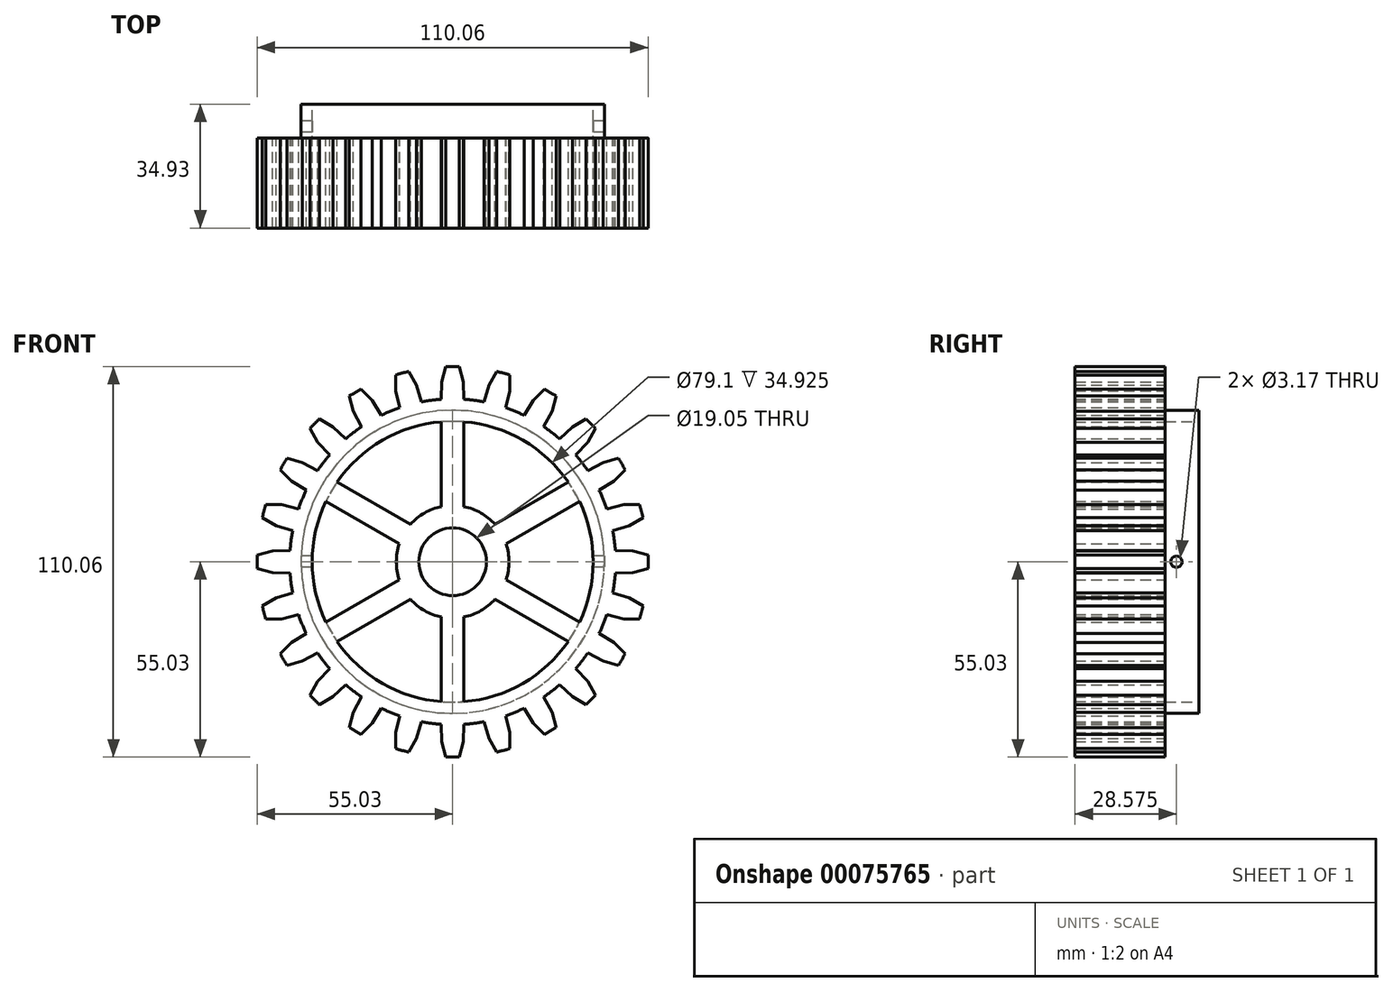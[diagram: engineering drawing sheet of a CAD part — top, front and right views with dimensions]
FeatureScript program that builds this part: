
annotation { "Feature Type Name" : "Feature", "Feature Type Description" : "" }
export const myFeature = defineFeature(function(context is Context, id is Id, definition is map)
    precondition{}
    {
        {
            var Q0;
            Q0=qCreatedBy(makeId("Front.planeOp"),FACE);
            var sketch = newSketch(context, id + "F0", { "sketchPlane" : qUnion([Q0])});
            skCircle(sketch, "E0", {"center": v(0, 0) * mm, "radius": 50.8 * mm, "construction": true});
            skCircle(sketch, "E1", {"center": v(0, 0) * mm, "radius": 45.9 * mm});
            skCircle(sketch, "E2", {"center": v(0, 0) * mm, "radius": 55.03 * mm});
            skLineSegment(sketch, "E3", {"start": v(-3.17, 45.8) * mm, "end": v(-3.05, 50.7) * mm});
            skLineSegment(sketch, "E4", {"start": v(-3.05, 50.7) * mm, "end": v(-1.9, 55) * mm});
            skLineSegment(sketch, "E5", {"start": v(3.18, 45.8) * mm, "end": v(3.05, 50.7) * mm});
            skLineSegment(sketch, "E6", {"start": v(3.05, 50.7) * mm, "end": v(1.9, 55) * mm});
            skLineSegment(sketch, "E7.1.0", {"start": v(-8.79, 45.05) * mm, "end": v(-10.18, 49.77) * mm});
            skLineSegment(sketch, "E7.1.1", {"start": v(-14.92, 43.41) * mm, "end": v(-16.07, 48.2) * mm});
            skLineSegment(sketch, "E7.1.2", {"start": v(-16.07, 48.2) * mm, "end": v(-16.08, 52.63) * mm});
            skLineSegment(sketch, "E7.1.3", {"start": v(-10.18, 49.77) * mm, "end": v(-12.4, 53.62) * mm});
            skLineSegment(sketch, "E7.2.0", {"start": v(-20.15, 41.24) * mm, "end": v(-22.71, 45.44) * mm});
            skLineSegment(sketch, "E7.2.1", {"start": v(-25.65, 38.07) * mm, "end": v(-28, 42.4) * mm});
            skLineSegment(sketch, "E7.2.2", {"start": v(-28, 42.4) * mm, "end": v(-29.15, 46.68) * mm});
            skLineSegment(sketch, "E7.2.3", {"start": v(-22.71, 45.44) * mm, "end": v(-25.85, 48.58) * mm});
            skLineSegment(sketch, "E7.3.0", {"start": v(-30.13, 34.62) * mm, "end": v(-33.7, 38.01) * mm});
            skLineSegment(sketch, "E7.3.1", {"start": v(-34.62, 30.13) * mm, "end": v(-38.01, 33.7) * mm});
            skLineSegment(sketch, "E7.3.2", {"start": v(-38.01, 33.7) * mm, "end": v(-40.24, 37.54) * mm});
            skLineSegment(sketch, "E7.3.3", {"start": v(-33.7, 38.01) * mm, "end": v(-37.54, 40.24) * mm});
            skLineSegment(sketch, "E7.4.0", {"start": v(-38.07, 25.65) * mm, "end": v(-42.4, 28) * mm});
            skLineSegment(sketch, "E7.4.1", {"start": v(-41.24, 20.15) * mm, "end": v(-45.44, 22.71) * mm});
            skLineSegment(sketch, "E7.4.2", {"start": v(-45.44, 22.71) * mm, "end": v(-48.58, 25.85) * mm});
            skLineSegment(sketch, "E7.4.3", {"start": v(-42.4, 28) * mm, "end": v(-46.68, 29.15) * mm});
            skLineSegment(sketch, "E7.5.0", {"start": v(-43.41, 14.92) * mm, "end": v(-48.2, 16.07) * mm});
            skLineSegment(sketch, "E7.5.1", {"start": v(-45.05, 8.79) * mm, "end": v(-49.77, 10.18) * mm});
            skLineSegment(sketch, "E7.5.2", {"start": v(-49.77, 10.18) * mm, "end": v(-53.62, 12.4) * mm});
            skLineSegment(sketch, "E7.5.3", {"start": v(-48.2, 16.07) * mm, "end": v(-52.63, 16.08) * mm});
            skLineSegment(sketch, "E7.6.0", {"start": v(-45.8, 3.18) * mm, "end": v(-50.7, 3.05) * mm});
            skLineSegment(sketch, "E7.6.1", {"start": v(-45.8, -3.17) * mm, "end": v(-50.7, -3.05) * mm});
            skLineSegment(sketch, "E7.6.2", {"start": v(-50.7, -3.05) * mm, "end": v(-55, -1.9) * mm});
            skLineSegment(sketch, "E7.6.3", {"start": v(-50.7, 3.05) * mm, "end": v(-55, 1.9) * mm});
            skLineSegment(sketch, "E7.7.0", {"start": v(-45.05, -8.79) * mm, "end": v(-49.77, -10.18) * mm});
            skLineSegment(sketch, "E7.7.1", {"start": v(-43.41, -14.92) * mm, "end": v(-48.2, -16.07) * mm});
            skLineSegment(sketch, "E7.7.2", {"start": v(-48.2, -16.07) * mm, "end": v(-52.63, -16.08) * mm});
            skLineSegment(sketch, "E7.7.3", {"start": v(-49.77, -10.18) * mm, "end": v(-53.62, -12.4) * mm});
            skLineSegment(sketch, "E7.8.0", {"start": v(-41.24, -20.15) * mm, "end": v(-45.44, -22.71) * mm});
            skLineSegment(sketch, "E7.8.1", {"start": v(-38.07, -25.65) * mm, "end": v(-42.4, -28) * mm});
            skLineSegment(sketch, "E7.8.2", {"start": v(-42.4, -28) * mm, "end": v(-46.68, -29.15) * mm});
            skLineSegment(sketch, "E7.8.3", {"start": v(-45.44, -22.71) * mm, "end": v(-48.58, -25.85) * mm});
            skLineSegment(sketch, "E7.9.0", {"start": v(-34.62, -30.13) * mm, "end": v(-38.01, -33.7) * mm});
            skLineSegment(sketch, "E7.9.1", {"start": v(-30.13, -34.62) * mm, "end": v(-33.7, -38.01) * mm});
            skLineSegment(sketch, "E7.9.2", {"start": v(-33.7, -38.01) * mm, "end": v(-37.54, -40.24) * mm});
            skLineSegment(sketch, "E7.9.3", {"start": v(-38.01, -33.7) * mm, "end": v(-40.24, -37.54) * mm});
            skLineSegment(sketch, "E7.10.0", {"start": v(-25.65, -38.07) * mm, "end": v(-28, -42.4) * mm});
            skLineSegment(sketch, "E7.10.1", {"start": v(-20.15, -41.24) * mm, "end": v(-22.71, -45.44) * mm});
            skLineSegment(sketch, "E7.10.2", {"start": v(-22.71, -45.44) * mm, "end": v(-25.85, -48.58) * mm});
            skLineSegment(sketch, "E7.10.3", {"start": v(-28, -42.4) * mm, "end": v(-29.15, -46.68) * mm});
            skLineSegment(sketch, "E7.11.0", {"start": v(-14.92, -43.41) * mm, "end": v(-16.07, -48.2) * mm});
            skLineSegment(sketch, "E7.11.1", {"start": v(-8.79, -45.05) * mm, "end": v(-10.18, -49.77) * mm});
            skLineSegment(sketch, "E7.11.2", {"start": v(-10.18, -49.77) * mm, "end": v(-12.4, -53.62) * mm});
            skLineSegment(sketch, "E7.11.3", {"start": v(-16.07, -48.2) * mm, "end": v(-16.08, -52.63) * mm});
            skLineSegment(sketch, "E7.12.0", {"start": v(-3.18, -45.8) * mm, "end": v(-3.05, -50.7) * mm});
            skLineSegment(sketch, "E7.12.1", {"start": v(3.17, -45.8) * mm, "end": v(3.05, -50.7) * mm});
            skLineSegment(sketch, "E7.12.2", {"start": v(3.05, -50.7) * mm, "end": v(1.9, -55) * mm});
            skLineSegment(sketch, "E7.12.3", {"start": v(-3.05, -50.7) * mm, "end": v(-1.9, -55) * mm});
            skLineSegment(sketch, "E7.13.0", {"start": v(8.79, -45.05) * mm, "end": v(10.18, -49.77) * mm});
            skLineSegment(sketch, "E7.13.1", {"start": v(14.92, -43.41) * mm, "end": v(16.07, -48.2) * mm});
            skLineSegment(sketch, "E7.13.2", {"start": v(16.07, -48.2) * mm, "end": v(16.08, -52.63) * mm});
            skLineSegment(sketch, "E7.13.3", {"start": v(10.18, -49.77) * mm, "end": v(12.4, -53.62) * mm});
            skLineSegment(sketch, "E7.14.0", {"start": v(20.15, -41.24) * mm, "end": v(22.71, -45.44) * mm});
            skLineSegment(sketch, "E7.14.1", {"start": v(25.65, -38.07) * mm, "end": v(28, -42.4) * mm});
            skLineSegment(sketch, "E7.14.2", {"start": v(28, -42.4) * mm, "end": v(29.15, -46.68) * mm});
            skLineSegment(sketch, "E7.14.3", {"start": v(22.71, -45.44) * mm, "end": v(25.85, -48.58) * mm});
            skLineSegment(sketch, "E7.15.0", {"start": v(30.13, -34.62) * mm, "end": v(33.7, -38.01) * mm});
            skLineSegment(sketch, "E7.15.1", {"start": v(34.62, -30.13) * mm, "end": v(38.01, -33.7) * mm});
            skLineSegment(sketch, "E7.15.2", {"start": v(38.01, -33.7) * mm, "end": v(40.24, -37.54) * mm});
            skLineSegment(sketch, "E7.15.3", {"start": v(33.7, -38.01) * mm, "end": v(37.54, -40.24) * mm});
            skLineSegment(sketch, "E7.16.0", {"start": v(38.07, -25.65) * mm, "end": v(42.4, -28) * mm});
            skLineSegment(sketch, "E7.16.1", {"start": v(41.24, -20.15) * mm, "end": v(45.44, -22.71) * mm});
            skLineSegment(sketch, "E7.16.2", {"start": v(45.44, -22.71) * mm, "end": v(48.58, -25.85) * mm});
            skLineSegment(sketch, "E7.16.3", {"start": v(42.4, -28) * mm, "end": v(46.68, -29.15) * mm});
            skLineSegment(sketch, "E7.17.0", {"start": v(43.41, -14.92) * mm, "end": v(48.2, -16.07) * mm});
            skLineSegment(sketch, "E7.17.1", {"start": v(45.05, -8.79) * mm, "end": v(49.77, -10.18) * mm});
            skLineSegment(sketch, "E7.17.2", {"start": v(49.77, -10.18) * mm, "end": v(53.62, -12.4) * mm});
            skLineSegment(sketch, "E7.17.3", {"start": v(48.2, -16.07) * mm, "end": v(52.63, -16.08) * mm});
            skLineSegment(sketch, "E7.18.0", {"start": v(45.8, -3.18) * mm, "end": v(50.7, -3.05) * mm});
            skLineSegment(sketch, "E7.18.1", {"start": v(45.8, 3.17) * mm, "end": v(50.7, 3.05) * mm});
            skLineSegment(sketch, "E7.18.2", {"start": v(50.7, 3.05) * mm, "end": v(55, 1.9) * mm});
            skLineSegment(sketch, "E7.18.3", {"start": v(50.7, -3.05) * mm, "end": v(55, -1.9) * mm});
            skLineSegment(sketch, "E7.19.0", {"start": v(45.05, 8.79) * mm, "end": v(49.77, 10.18) * mm});
            skLineSegment(sketch, "E7.19.1", {"start": v(43.41, 14.92) * mm, "end": v(48.2, 16.07) * mm});
            skLineSegment(sketch, "E7.19.2", {"start": v(48.2, 16.07) * mm, "end": v(52.63, 16.08) * mm});
            skLineSegment(sketch, "E7.19.3", {"start": v(49.77, 10.18) * mm, "end": v(53.62, 12.4) * mm});
            skLineSegment(sketch, "E7.20.0", {"start": v(41.24, 20.15) * mm, "end": v(45.44, 22.71) * mm});
            skLineSegment(sketch, "E7.20.1", {"start": v(38.07, 25.65) * mm, "end": v(42.4, 28) * mm});
            skLineSegment(sketch, "E7.20.2", {"start": v(42.4, 28) * mm, "end": v(46.68, 29.15) * mm});
            skLineSegment(sketch, "E7.20.3", {"start": v(45.44, 22.71) * mm, "end": v(48.58, 25.85) * mm});
            skLineSegment(sketch, "E7.21.0", {"start": v(34.62, 30.13) * mm, "end": v(38.01, 33.7) * mm});
            skLineSegment(sketch, "E7.21.1", {"start": v(30.13, 34.62) * mm, "end": v(33.7, 38.01) * mm});
            skLineSegment(sketch, "E7.21.2", {"start": v(33.7, 38.01) * mm, "end": v(37.54, 40.24) * mm});
            skLineSegment(sketch, "E7.21.3", {"start": v(38.01, 33.7) * mm, "end": v(40.24, 37.54) * mm});
            skLineSegment(sketch, "E7.22.0", {"start": v(25.65, 38.07) * mm, "end": v(28, 42.4) * mm});
            skLineSegment(sketch, "E7.22.1", {"start": v(20.15, 41.24) * mm, "end": v(22.71, 45.44) * mm});
            skLineSegment(sketch, "E7.22.2", {"start": v(22.71, 45.44) * mm, "end": v(25.85, 48.58) * mm});
            skLineSegment(sketch, "E7.22.3", {"start": v(28, 42.4) * mm, "end": v(29.15, 46.68) * mm});
            skLineSegment(sketch, "E7.23.0", {"start": v(14.92, 43.41) * mm, "end": v(16.07, 48.2) * mm});
            skLineSegment(sketch, "E7.23.1", {"start": v(8.79, 45.05) * mm, "end": v(10.18, 49.77) * mm});
            skLineSegment(sketch, "E7.23.2", {"start": v(10.18, 49.77) * mm, "end": v(12.4, 53.62) * mm});
            skLineSegment(sketch, "E7.23.3", {"start": v(16.07, 48.2) * mm, "end": v(16.08, 52.63) * mm});
            skSolve(sketch);
        }
        {
            var Q0;
            {var subQ18=sQuery(id+"F0.wireOp",EDGE,"827518fb-3b91-4696-8486-c9bf2b698782.1.2");Q0=makeQuery(id+"F0.imprint","IMPRINT",FACE,{"disambiguationData":[TD([[makeQuery(id+"F0.imprint","IMPRINT",EDGE,{"derivedFrom":subQ18}),1.0]])]});}
            var Q1;
            {var subQ1=sQuery(id+"F0.wireOp",EDGE,"827518fb-3b91-4696-8486-c9bf2b698782.7.0");Q1=makeQuery(id+"F0.imprint","IMPRINT",FACE,{"disambiguationData":[TD([[makeQuery(id+"F0.imprint","IMPRINT",EDGE,{"derivedFrom":subQ1}),-1.0]])]});}
            var Q2;
            {var subQ1=sQuery(id+"F0.wireOp",EDGE,"827518fb-3b91-4696-8486-c9bf2b698782.8.0");Q2=makeQuery(id+"F0.imprint","IMPRINT",FACE,{"disambiguationData":[TD([[makeQuery(id+"F0.imprint","IMPRINT",EDGE,{"derivedFrom":subQ1}),-1.0]])]});}
            var Q3;
            {var subQ1=sQuery(id+"F0.wireOp",EDGE,"827518fb-3b91-4696-8486-c9bf2b698782.9.0");Q3=makeQuery(id+"F0.imprint","IMPRINT",FACE,{"disambiguationData":[TD([[makeQuery(id+"F0.imprint","IMPRINT",EDGE,{"derivedFrom":subQ1}),-1.0]])]});}
            var Q4;
            {var subQ1=sQuery(id+"F0.wireOp",EDGE,"827518fb-3b91-4696-8486-c9bf2b698782.6.0");Q4=makeQuery(id+"F0.imprint","IMPRINT",FACE,{"disambiguationData":[TD([[makeQuery(id+"F0.imprint","IMPRINT",EDGE,{"derivedFrom":subQ1}),-1.0]])]});}
            var Q5;
            {var subQ1=sQuery(id+"F0.wireOp",EDGE,"9a822041-26f0-4712-b48c-d55ef83ccb79.1.13.0");Q5=makeQuery(id+"F0.imprint","IMPRINT",FACE,{"disambiguationData":[TD([[makeQuery(id+"F0.imprint","IMPRINT",EDGE,{"derivedFrom":subQ1}),-1.0]])]});}
            var Q6;
            {var subQ1=sQuery(id+"F0.wireOp",EDGE,"9a822041-26f0-4712-b48c-d55ef83ccb79.1.15.0");Q6=makeQuery(id+"F0.imprint","IMPRINT",FACE,{"disambiguationData":[TD([[makeQuery(id+"F0.imprint","IMPRINT",EDGE,{"derivedFrom":subQ1}),-1.0]])]});}
            var Q7;
            {var subQ1=sQuery(id+"F0.wireOp",EDGE,"9a822041-26f0-4712-b48c-d55ef83ccb79.1.14.0");Q7=makeQuery(id+"F0.imprint","IMPRINT",FACE,{"disambiguationData":[TD([[makeQuery(id+"F0.imprint","IMPRINT",EDGE,{"derivedFrom":subQ1}),-1.0]])]});}
            var Q8;
            {var subQ1=sQuery(id+"F0.wireOp",EDGE,"9a822041-26f0-4712-b48c-d55ef83ccb79.1.12.0");Q8=makeQuery(id+"F0.imprint","IMPRINT",FACE,{"disambiguationData":[TD([[makeQuery(id+"F0.imprint","IMPRINT",EDGE,{"derivedFrom":subQ1}),-1.0]])]});}
            var Q9;
            {var subQ1=sQuery(id+"F0.wireOp",EDGE,"827518fb-3b91-4696-8486-c9bf2b698782.2.0");Q9=makeQuery(id+"F0.imprint","IMPRINT",FACE,{"disambiguationData":[TD([[makeQuery(id+"F0.imprint","IMPRINT",EDGE,{"derivedFrom":subQ1}),-1.0]])]});}
            var Q10;
            {var subQ1=sQuery(id+"F0.wireOp",EDGE,"827518fb-3b91-4696-8486-c9bf2b698782.1.0");Q10=makeQuery(id+"F0.imprint","IMPRINT",FACE,{"disambiguationData":[TD([[makeQuery(id+"F0.imprint","IMPRINT",EDGE,{"derivedFrom":subQ1}),-1.0]])]});}
            var Q11;
            {var subQ1=sQuery(id+"F0.wireOp",EDGE,"9a822041-26f0-4712-b48c-d55ef83ccb79.1.23.0");Q11=makeQuery(id+"F0.imprint","IMPRINT",FACE,{"disambiguationData":[TD([[makeQuery(id+"F0.imprint","IMPRINT",EDGE,{"derivedFrom":subQ1}),-1.0]])]});}
            var Q12;
            {var subQ1=sQuery(id+"F0.wireOp",EDGE,"9a822041-26f0-4712-b48c-d55ef83ccb79.1.22.0");Q12=makeQuery(id+"F0.imprint","IMPRINT",FACE,{"disambiguationData":[TD([[makeQuery(id+"F0.imprint","IMPRINT",EDGE,{"derivedFrom":subQ1}),-1.0]])]});}
            var Q13;
            {var subQ1=sQuery(id+"F0.wireOp",EDGE,"9a822041-26f0-4712-b48c-d55ef83ccb79.1.21.0");Q13=makeQuery(id+"F0.imprint","IMPRINT",FACE,{"disambiguationData":[TD([[makeQuery(id+"F0.imprint","IMPRINT",EDGE,{"derivedFrom":subQ1}),-1.0]])]});}
            var Q14;
            {var subQ1=sQuery(id+"F0.wireOp",EDGE,"9a822041-26f0-4712-b48c-d55ef83ccb79.1.17.0");Q14=makeQuery(id+"F0.imprint","IMPRINT",FACE,{"disambiguationData":[TD([[makeQuery(id+"F0.imprint","IMPRINT",EDGE,{"derivedFrom":subQ1}),-1.0]])]});}
            var Q15;
            {var subQ1=sQuery(id+"F0.wireOp",EDGE,"9a822041-26f0-4712-b48c-d55ef83ccb79.1.16.0");Q15=makeQuery(id+"F0.imprint","IMPRINT",FACE,{"disambiguationData":[TD([[makeQuery(id+"F0.imprint","IMPRINT",EDGE,{"derivedFrom":subQ1}),-1.0]])]});}
            var Q16;
            {var subQ1=sQuery(id+"F0.wireOp",EDGE,"827518fb-3b91-4696-8486-c9bf2b698782.11.0");Q16=makeQuery(id+"F0.imprint","IMPRINT",FACE,{"disambiguationData":[TD([[makeQuery(id+"F0.imprint","IMPRINT",EDGE,{"derivedFrom":subQ1}),-1.0]])]});}
            var Q17;
            {var subQ1=sQuery(id+"F0.wireOp",EDGE,"827518fb-3b91-4696-8486-c9bf2b698782.10.0");Q17=makeQuery(id+"F0.imprint","IMPRINT",FACE,{"disambiguationData":[TD([[makeQuery(id+"F0.imprint","IMPRINT",EDGE,{"derivedFrom":subQ1}),-1.0]])]});}
            var Q18;
            {var subQ0=sQuery(id+"F0.wireOp",EDGE,"9a822041-26f0-4712-b48c-d55ef83ccb79.6.21.0");Q18=makeQuery(id+"F0.imprint","IMPRINT",FACE,{"disambiguationData":[TD([[makeQuery(id+"F0.imprint","IMPRINT",EDGE,{"derivedFrom":subQ0}),-1.0]])]});}
            var Q19;
            {var subQ0=sQuery(id+"F0.wireOp",EDGE,"827518fb-3b91-4696-8486-c9bf2b698782.1.2");Q19=makeQuery(id+"F0.imprint","IMPRINT",FACE,{"disambiguationData":[TD([[makeQuery(id+"F0.imprint","IMPRINT",EDGE,{"derivedFrom":subQ0}),-1.0]])]});}
            var Q20;
            {var subQ0=sQuery(id+"F0.wireOp",EDGE,"827518fb-3b91-4696-8486-c9bf2b698782.8.2");Q20=makeQuery(id+"F0.imprint","IMPRINT",FACE,{"disambiguationData":[TD([[makeQuery(id+"F0.imprint","IMPRINT",EDGE,{"derivedFrom":subQ0}),-1.0]])]});}
            var Q21;
            {var subQ0=sQuery(id+"F0.wireOp",EDGE,"9a822041-26f0-4712-b48c-d55ef83ccb79.6.15.0");Q21=makeQuery(id+"F0.imprint","IMPRINT",FACE,{"disambiguationData":[TD([[makeQuery(id+"F0.imprint","IMPRINT",EDGE,{"derivedFrom":subQ0}),-1.0]])]});}
            var Q22;
            {var subQ0=sQuery(id+"F0.wireOp",EDGE,"827518fb-3b91-4696-8486-c9bf2b698782.6.2");Q22=makeQuery(id+"F0.imprint","IMPRINT",FACE,{"disambiguationData":[TD([[makeQuery(id+"F0.imprint","IMPRINT",EDGE,{"derivedFrom":subQ0}),-1.0]])]});}
            var Q23;
            {var subQ0=sQuery(id+"F0.wireOp",EDGE,"827518fb-3b91-4696-8486-c9bf2b698782.9.2");Q23=makeQuery(id+"F0.imprint","IMPRINT",FACE,{"disambiguationData":[TD([[makeQuery(id+"F0.imprint","IMPRINT",EDGE,{"derivedFrom":subQ0}),-1.0]])]});}
            var Q24;
            {var subQ0=sQuery(id+"F0.wireOp",EDGE,"9a822041-26f0-4712-b48c-d55ef83ccb79.6.16.0");Q24=makeQuery(id+"F0.imprint","IMPRINT",FACE,{"disambiguationData":[TD([[makeQuery(id+"F0.imprint","IMPRINT",EDGE,{"derivedFrom":subQ0}),-1.0]])]});}
            var Q25;
            {var subQ0=sQuery(id+"F0.wireOp",EDGE,"9a822041-26f0-4712-b48c-d55ef83ccb79.6.13.0");Q25=makeQuery(id+"F0.imprint","IMPRINT",FACE,{"disambiguationData":[TD([[makeQuery(id+"F0.imprint","IMPRINT",EDGE,{"derivedFrom":subQ0}),-1.0]])]});}
            var Q26;
            {var subQ1=sQuery(id+"F0.wireOp",EDGE,"827518fb-3b91-4696-8486-c9bf2b698782.5.0");Q26=makeQuery(id+"F0.imprint","IMPRINT",FACE,{"disambiguationData":[TD([[makeQuery(id+"F0.imprint","IMPRINT",EDGE,{"derivedFrom":subQ1}),-1.0]])]});}
            var Q27;
            {var subQ1=sQuery(id+"F0.wireOp",EDGE,"827518fb-3b91-4696-8486-c9bf2b698782.4.0");Q27=makeQuery(id+"F0.imprint","IMPRINT",FACE,{"disambiguationData":[TD([[makeQuery(id+"F0.imprint","IMPRINT",EDGE,{"derivedFrom":subQ1}),-1.0]])]});}
            var Q28;
            {var subQ1=sQuery(id+"F0.wireOp",EDGE,"827518fb-3b91-4696-8486-c9bf2b698782.3.0");Q28=makeQuery(id+"F0.imprint","IMPRINT",FACE,{"disambiguationData":[TD([[makeQuery(id+"F0.imprint","IMPRINT",EDGE,{"derivedFrom":subQ1}),-1.0]])]});}
            var Q29;
            {var subQ1=sQuery(id+"F0.wireOp",EDGE,"9a822041-26f0-4712-b48c-d55ef83ccb79.1.20.0");Q29=makeQuery(id+"F0.imprint","IMPRINT",FACE,{"disambiguationData":[TD([[makeQuery(id+"F0.imprint","IMPRINT",EDGE,{"derivedFrom":subQ1}),-1.0]])]});}
            var Q30;
            {var subQ1=sQuery(id+"F0.wireOp",EDGE,"9a822041-26f0-4712-b48c-d55ef83ccb79.1.19.0");Q30=makeQuery(id+"F0.imprint","IMPRINT",FACE,{"disambiguationData":[TD([[makeQuery(id+"F0.imprint","IMPRINT",EDGE,{"derivedFrom":subQ1}),-1.0]])]});}
            var Q31;
            {var subQ1=sQuery(id+"F0.wireOp",EDGE,"9a822041-26f0-4712-b48c-d55ef83ccb79.1.18.0");Q31=makeQuery(id+"F0.imprint","IMPRINT",FACE,{"disambiguationData":[TD([[makeQuery(id+"F0.imprint","IMPRINT",EDGE,{"derivedFrom":subQ1}),-1.0]])]});}
            var Q32;
            {var subQ0=sQuery(id+"F0.wireOp",EDGE,"827518fb-3b91-4696-8486-c9bf2b698782.5.2");Q32=makeQuery(id+"F0.imprint","IMPRINT",FACE,{"disambiguationData":[TD([[makeQuery(id+"F0.imprint","IMPRINT",EDGE,{"derivedFrom":subQ0}),-1.0]])]});}
            var Q33;
            {var subQ0=sQuery(id+"F0.wireOp",EDGE,"9a822041-26f0-4712-b48c-d55ef83ccb79.6.18.0");Q33=makeQuery(id+"F0.imprint","IMPRINT",FACE,{"disambiguationData":[TD([[makeQuery(id+"F0.imprint","IMPRINT",EDGE,{"derivedFrom":subQ0}),-1.0]])]});}
            var Q34;
            {var subQ0=sQuery(id+"F0.wireOp",EDGE,"827518fb-3b91-4696-8486-c9bf2b698782.11.2");Q34=makeQuery(id+"F0.imprint","IMPRINT",FACE,{"disambiguationData":[TD([[makeQuery(id+"F0.imprint","IMPRINT",EDGE,{"derivedFrom":subQ0}),-1.0]])]});}
            var Q35;
            {var subQ0=sQuery(id+"F0.wireOp",EDGE,"827518fb-3b91-4696-8486-c9bf2b698782.4.2");Q35=makeQuery(id+"F0.imprint","IMPRINT",FACE,{"disambiguationData":[TD([[makeQuery(id+"F0.imprint","IMPRINT",EDGE,{"derivedFrom":subQ0}),-1.0]])]});}
            var Q36;
            {var subQ0=sQuery(id+"F0.wireOp",EDGE,"9a822041-26f0-4712-b48c-d55ef83ccb79.6.17.0");Q36=makeQuery(id+"F0.imprint","IMPRINT",FACE,{"disambiguationData":[TD([[makeQuery(id+"F0.imprint","IMPRINT",EDGE,{"derivedFrom":subQ0}),-1.0]])]});}
            var Q37;
            {var subQ0=sQuery(id+"F0.wireOp",EDGE,"827518fb-3b91-4696-8486-c9bf2b698782.3.2");Q37=makeQuery(id+"F0.imprint","IMPRINT",FACE,{"disambiguationData":[TD([[makeQuery(id+"F0.imprint","IMPRINT",EDGE,{"derivedFrom":subQ0}),-1.0]])]});}
            var Q38;
            {var subQ0=sQuery(id+"F0.wireOp",EDGE,"9a822041-26f0-4712-b48c-d55ef83ccb79.6.14.0");Q38=makeQuery(id+"F0.imprint","IMPRINT",FACE,{"disambiguationData":[TD([[makeQuery(id+"F0.imprint","IMPRINT",EDGE,{"derivedFrom":subQ0}),-1.0]])]});}
            var Q39;
            {var subQ0=sQuery(id+"F0.wireOp",EDGE,"9a822041-26f0-4712-b48c-d55ef83ccb79.6.22.0");Q39=makeQuery(id+"F0.imprint","IMPRINT",FACE,{"disambiguationData":[TD([[makeQuery(id+"F0.imprint","IMPRINT",EDGE,{"derivedFrom":subQ0}),-1.0]])]});}
            var Q40;
            {var subQ0=sQuery(id+"F0.wireOp",EDGE,"827518fb-3b91-4696-8486-c9bf2b698782.2.2");Q40=makeQuery(id+"F0.imprint","IMPRINT",FACE,{"disambiguationData":[TD([[makeQuery(id+"F0.imprint","IMPRINT",EDGE,{"derivedFrom":subQ0}),-1.0]])]});}
            var Q41;
            {var subQ0=sQuery(id+"F0.wireOp",EDGE,"9a822041-26f0-4712-b48c-d55ef83ccb79.6.23.0");Q41=makeQuery(id+"F0.imprint","IMPRINT",FACE,{"disambiguationData":[TD([[makeQuery(id+"F0.imprint","IMPRINT",EDGE,{"derivedFrom":subQ0}),-1.0]])]});}
            var Q42;
            {var subQ0=sQuery(id+"F0.wireOp",EDGE,"827518fb-3b91-4696-8486-c9bf2b698782.7.2");Q42=makeQuery(id+"F0.imprint","IMPRINT",FACE,{"disambiguationData":[TD([[makeQuery(id+"F0.imprint","IMPRINT",EDGE,{"derivedFrom":subQ0}),-1.0]])]});}
            var Q43;
            {var subQ0=sQuery(id+"F0.wireOp",EDGE,"9a822041-26f0-4712-b48c-d55ef83ccb79.6.19.0");Q43=makeQuery(id+"F0.imprint","IMPRINT",FACE,{"disambiguationData":[TD([[makeQuery(id+"F0.imprint","IMPRINT",EDGE,{"derivedFrom":subQ0}),-1.0]])]});}
            var Q44;
            {var subQ0=sQuery(id+"F0.wireOp",EDGE,"9a822041-26f0-4712-b48c-d55ef83ccb79.6.12.0");Q44=makeQuery(id+"F0.imprint","IMPRINT",FACE,{"disambiguationData":[TD([[makeQuery(id+"F0.imprint","IMPRINT",EDGE,{"derivedFrom":subQ0}),-1.0]])]});}
            var Q45;
            {var subQ0=sQuery(id+"F0.wireOp",EDGE,"9a822041-26f0-4712-b48c-d55ef83ccb79.6.20.0");Q45=makeQuery(id+"F0.imprint","IMPRINT",FACE,{"disambiguationData":[TD([[makeQuery(id+"F0.imprint","IMPRINT",EDGE,{"derivedFrom":subQ0}),-1.0]])]});}
            var Q46;
            {var subQ0=sQuery(id+"F0.wireOp",EDGE,"827518fb-3b91-4696-8486-c9bf2b698782.10.2");Q46=makeQuery(id+"F0.imprint","IMPRINT",FACE,{"disambiguationData":[TD([[makeQuery(id+"F0.imprint","IMPRINT",EDGE,{"derivedFrom":subQ0}),-1.0]])]});}
            var Q47;
            {var subQ1=sQuery(id+"F0.wireOp",EDGE,"E7.4.0");Q47=makeQuery(id+"F0.imprint","IMPRINT",FACE,{"disambiguationData":[TD([[makeQuery(id+"F0.imprint","IMPRINT",EDGE,{"derivedFrom":subQ1}),1.0]])]});}
            var Q48;
            {var subQ0=sQuery(id+"F0.wireOp",EDGE,"E1");var subQ30=makeQuery(id+"F0.imprint","INTERSECT",VERTEX,{"derivedFrom":[subQ0,sQuery(id+"F0.wireOp",EDGE,"E7.18.1")]});Q48=makeQuery(id+"F0.imprint","IMPRINT",FACE,{"disambiguationData":[TD([[makeQuery(id+"F0.imprint","IMPRINT",EDGE,{"disambiguationData":[TD([[subQ30,-1.0]])],"derivedFrom":subQ0}),1.0]])]});}
            var Q49;
            {var subQ1=sQuery(id+"F0.wireOp",EDGE,"E7.3.0");Q49=makeQuery(id+"F0.imprint","IMPRINT",FACE,{"disambiguationData":[TD([[makeQuery(id+"F0.imprint","IMPRINT",EDGE,{"derivedFrom":subQ1}),1.0]])]});}
            var Q50;
            {var subQ4=sQuery(id+"F0.wireOp",EDGE,"E7.2.0");Q50=makeQuery(id+"F0.imprint","IMPRINT",FACE,{"disambiguationData":[TD([[makeQuery(id+"F0.imprint","IMPRINT",EDGE,{"derivedFrom":subQ4}),1.0]])]});}
            var Q51;
            {var subQ1=sQuery(id+"F0.wireOp",EDGE,"E7.1.0");Q51=makeQuery(id+"F0.imprint","IMPRINT",FACE,{"disambiguationData":[TD([[makeQuery(id+"F0.imprint","IMPRINT",EDGE,{"derivedFrom":subQ1}),1.0]])]});}
            var Q52;
            {var subQ2=sQuery(id+"F0.wireOp",EDGE,"E3");Q52=makeQuery(id+"F0.imprint","IMPRINT",FACE,{"disambiguationData":[TD([[makeQuery(id+"F0.imprint","IMPRINT",EDGE,{"derivedFrom":subQ2}),-1.0]])]});}
            var Q53;
            {var subQ4=sQuery(id+"F0.wireOp",EDGE,"E7.23.0");Q53=makeQuery(id+"F0.imprint","IMPRINT",FACE,{"disambiguationData":[TD([[makeQuery(id+"F0.imprint","IMPRINT",EDGE,{"derivedFrom":subQ4}),1.0]])]});}
            var Q54;
            {var subQ1=sQuery(id+"F0.wireOp",EDGE,"E7.22.0");Q54=makeQuery(id+"F0.imprint","IMPRINT",FACE,{"disambiguationData":[TD([[makeQuery(id+"F0.imprint","IMPRINT",EDGE,{"derivedFrom":subQ1}),1.0]])]});}
            var Q55;
            {var subQ4=sQuery(id+"F0.wireOp",EDGE,"E7.21.0");Q55=makeQuery(id+"F0.imprint","IMPRINT",FACE,{"disambiguationData":[TD([[makeQuery(id+"F0.imprint","IMPRINT",EDGE,{"derivedFrom":subQ4}),1.0]])]});}
            var Q56;
            {var subQ4=sQuery(id+"F0.wireOp",EDGE,"E7.20.0");Q56=makeQuery(id+"F0.imprint","IMPRINT",FACE,{"disambiguationData":[TD([[makeQuery(id+"F0.imprint","IMPRINT",EDGE,{"derivedFrom":subQ4}),1.0]])]});}
            var Q57;
            {var subQ2=sQuery(id+"F0.wireOp",EDGE,"E7.19.0");Q57=makeQuery(id+"F0.imprint","IMPRINT",FACE,{"disambiguationData":[TD([[makeQuery(id+"F0.imprint","IMPRINT",EDGE,{"derivedFrom":subQ2}),1.0]])]});}
            var Q58;
            {var subQ3=sQuery(id+"F0.wireOp",EDGE,"E7.18.0");Q58=makeQuery(id+"F0.imprint","IMPRINT",FACE,{"disambiguationData":[TD([[makeQuery(id+"F0.imprint","IMPRINT",EDGE,{"derivedFrom":subQ3}),1.0]])]});}
            var Q59;
            {var subQ1=sQuery(id+"F0.wireOp",EDGE,"E7.17.0");Q59=makeQuery(id+"F0.imprint","IMPRINT",FACE,{"disambiguationData":[TD([[makeQuery(id+"F0.imprint","IMPRINT",EDGE,{"derivedFrom":subQ1}),1.0]])]});}
            var Q60;
            {var subQ1=sQuery(id+"F0.wireOp",EDGE,"E7.16.0");Q60=makeQuery(id+"F0.imprint","IMPRINT",FACE,{"disambiguationData":[TD([[makeQuery(id+"F0.imprint","IMPRINT",EDGE,{"derivedFrom":subQ1}),1.0]])]});}
            var Q61;
            {var subQ4=sQuery(id+"F0.wireOp",EDGE,"E7.15.0");Q61=makeQuery(id+"F0.imprint","IMPRINT",FACE,{"disambiguationData":[TD([[makeQuery(id+"F0.imprint","IMPRINT",EDGE,{"derivedFrom":subQ4}),1.0]])]});}
            var Q62;
            {var subQ4=sQuery(id+"F0.wireOp",EDGE,"E7.14.0");Q62=makeQuery(id+"F0.imprint","IMPRINT",FACE,{"disambiguationData":[TD([[makeQuery(id+"F0.imprint","IMPRINT",EDGE,{"derivedFrom":subQ4}),1.0]])]});}
            var Q63;
            {var subQ4=sQuery(id+"F0.wireOp",EDGE,"E7.13.0");Q63=makeQuery(id+"F0.imprint","IMPRINT",FACE,{"disambiguationData":[TD([[makeQuery(id+"F0.imprint","IMPRINT",EDGE,{"derivedFrom":subQ4}),1.0]])]});}
            var Q64;
            {var subQ4=sQuery(id+"F0.wireOp",EDGE,"E7.12.0");Q64=makeQuery(id+"F0.imprint","IMPRINT",FACE,{"disambiguationData":[TD([[makeQuery(id+"F0.imprint","IMPRINT",EDGE,{"derivedFrom":subQ4}),1.0]])]});}
            var Q65;
            {var subQ1=sQuery(id+"F0.wireOp",EDGE,"E7.11.0");Q65=makeQuery(id+"F0.imprint","IMPRINT",FACE,{"disambiguationData":[TD([[makeQuery(id+"F0.imprint","IMPRINT",EDGE,{"derivedFrom":subQ1}),1.0]])]});}
            var Q66;
            {var subQ1=sQuery(id+"F0.wireOp",EDGE,"E7.10.0");Q66=makeQuery(id+"F0.imprint","IMPRINT",FACE,{"disambiguationData":[TD([[makeQuery(id+"F0.imprint","IMPRINT",EDGE,{"derivedFrom":subQ1}),1.0]])]});}
            var Q67;
            {var subQ1=sQuery(id+"F0.wireOp",EDGE,"E7.9.0");Q67=makeQuery(id+"F0.imprint","IMPRINT",FACE,{"disambiguationData":[TD([[makeQuery(id+"F0.imprint","IMPRINT",EDGE,{"derivedFrom":subQ1}),1.0]])]});}
            var Q68;
            {var subQ1=sQuery(id+"F0.wireOp",EDGE,"E7.8.0");Q68=makeQuery(id+"F0.imprint","IMPRINT",FACE,{"disambiguationData":[TD([[makeQuery(id+"F0.imprint","IMPRINT",EDGE,{"derivedFrom":subQ1}),1.0]])]});}
            var Q69;
            {var subQ0=sQuery(id+"F0.wireOp",EDGE,"E7.7.0");Q69=makeQuery(id+"F0.imprint","IMPRINT",FACE,{"disambiguationData":[TD([[makeQuery(id+"F0.imprint","IMPRINT",EDGE,{"derivedFrom":subQ0}),1.0]])]});}
            var Q70;
            {var subQ1=sQuery(id+"F0.wireOp",EDGE,"E7.6.0");Q70=makeQuery(id+"F0.imprint","IMPRINT",FACE,{"disambiguationData":[TD([[makeQuery(id+"F0.imprint","IMPRINT",EDGE,{"derivedFrom":subQ1}),1.0]])]});}
            var Q71;
            {var subQ0=sQuery(id+"F0.wireOp",EDGE,"E7.5.0");Q71=makeQuery(id+"F0.imprint","IMPRINT",FACE,{"disambiguationData":[TD([[makeQuery(id+"F0.imprint","IMPRINT",EDGE,{"derivedFrom":subQ0}),1.0]])]});}
            extrude(context, id + "F1", {"entities" : qUnion([Q0, Q1, Q2, Q3, Q4, Q5, Q6, Q7, Q8, Q9, Q10, Q11, Q12, Q13, Q14, Q15, Q16, Q17, Q18, Q19, Q20, Q21, Q22, Q23, Q24, Q25, Q26, Q27, Q28, Q29, Q30, Q31, Q32, Q33, Q34, Q35, Q36, Q37, Q38, Q39, Q40, Q41, Q42, Q43, Q44, Q45, Q46, Q47, Q48, Q49, Q50, Q51, Q52, Q53, Q54, Q55, Q56, Q57, Q58, Q59, Q60, Q61, Q62, Q63, Q64, Q65, Q66, Q67, Q68, Q69, Q70, Q71]), "endBound" : BoundingType.SYMMETRIC, "depth" : 25.4 * mm});
        }
        {
            var Q0;
            Q0=qCreatedBy(makeId("Front.planeOp"),FACE);
            var sketch = newSketch(context, id + "F2", { "sketchPlane" : qUnion([Q0])});
            skCircle(sketch, "E8", {"center": v(0, 0) * mm, "radius": 9.53 * mm});
            skSolve(sketch);
        }
        {
            var Q0;
            Q0 = qSketchRegion(id + "F2", true);
            extrude(context, id + "F3", {"entities" : qUnion([Q0]), "operationType" : NewBodyOperationType.REMOVE, "endBound" : BoundingType.SYMMETRIC, "depth" : 50.8 * mm});
        }
        {
            var Q0;
            Q0=makeQuery(id+"F1.opExtrude","CAP_FACE",FACE,{"disambiguationData":[OSD([sQuery(id+"F0.wireOp",EDGE,"E1"),sQuery(id+"F0.wireOp",EDGE,"E2"),sQuery(id+"F0.wireOp",EDGE,"E3"),sQuery(id+"F0.wireOp",EDGE,"E4"),sQuery(id+"F0.wireOp",EDGE,"E5"),sQuery(id+"F0.wireOp",EDGE,"E6"),sQuery(id+"F0.wireOp",EDGE,"E7.1.0"),sQuery(id+"F0.wireOp",EDGE,"E7.1.1"),sQuery(id+"F0.wireOp",EDGE,"E7.1.2"),sQuery(id+"F0.wireOp",EDGE,"E7.1.3"),sQuery(id+"F0.wireOp",EDGE,"E7.2.0"),sQuery(id+"F0.wireOp",EDGE,"E7.2.1"),sQuery(id+"F0.wireOp",EDGE,"E7.2.2"),sQuery(id+"F0.wireOp",EDGE,"E7.2.3"),sQuery(id+"F0.wireOp",EDGE,"E7.3.0"),sQuery(id+"F0.wireOp",EDGE,"E7.3.1"),sQuery(id+"F0.wireOp",EDGE,"E7.3.2"),sQuery(id+"F0.wireOp",EDGE,"E7.3.3"),sQuery(id+"F0.wireOp",EDGE,"E7.4.0"),sQuery(id+"F0.wireOp",EDGE,"E7.4.1"),sQuery(id+"F0.wireOp",EDGE,"E7.4.2"),sQuery(id+"F0.wireOp",EDGE,"E7.4.3"),sQuery(id+"F0.wireOp",EDGE,"E7.5.0"),sQuery(id+"F0.wireOp",EDGE,"E7.5.1"),sQuery(id+"F0.wireOp",EDGE,"E7.5.2"),sQuery(id+"F0.wireOp",EDGE,"E7.5.3"),sQuery(id+"F0.wireOp",EDGE,"E7.6.0"),sQuery(id+"F0.wireOp",EDGE,"E7.6.1"),sQuery(id+"F0.wireOp",EDGE,"E7.6.2"),sQuery(id+"F0.wireOp",EDGE,"E7.6.3"),sQuery(id+"F0.wireOp",EDGE,"E7.7.0"),sQuery(id+"F0.wireOp",EDGE,"E7.7.1"),sQuery(id+"F0.wireOp",EDGE,"E7.7.2"),sQuery(id+"F0.wireOp",EDGE,"E7.7.3"),sQuery(id+"F0.wireOp",EDGE,"E7.8.0"),sQuery(id+"F0.wireOp",EDGE,"E7.8.1"),sQuery(id+"F0.wireOp",EDGE,"E7.8.2"),sQuery(id+"F0.wireOp",EDGE,"E7.8.3"),sQuery(id+"F0.wireOp",EDGE,"E7.9.0"),sQuery(id+"F0.wireOp",EDGE,"E7.9.1"),sQuery(id+"F0.wireOp",EDGE,"E7.9.2"),sQuery(id+"F0.wireOp",EDGE,"E7.9.3"),sQuery(id+"F0.wireOp",EDGE,"E7.10.0"),sQuery(id+"F0.wireOp",EDGE,"E7.10.1"),sQuery(id+"F0.wireOp",EDGE,"E7.10.2"),sQuery(id+"F0.wireOp",EDGE,"E7.10.3"),sQuery(id+"F0.wireOp",EDGE,"E7.11.0"),sQuery(id+"F0.wireOp",EDGE,"E7.11.1"),sQuery(id+"F0.wireOp",EDGE,"E7.11.2"),sQuery(id+"F0.wireOp",EDGE,"E7.11.3"),sQuery(id+"F0.wireOp",EDGE,"E7.12.0"),sQuery(id+"F0.wireOp",EDGE,"E7.12.1"),sQuery(id+"F0.wireOp",EDGE,"E7.12.2"),sQuery(id+"F0.wireOp",EDGE,"E7.12.3"),sQuery(id+"F0.wireOp",EDGE,"E7.13.0"),sQuery(id+"F0.wireOp",EDGE,"E7.13.1"),sQuery(id+"F0.wireOp",EDGE,"E7.13.2"),sQuery(id+"F0.wireOp",EDGE,"E7.13.3"),sQuery(id+"F0.wireOp",EDGE,"E7.14.0"),sQuery(id+"F0.wireOp",EDGE,"E7.14.1"),sQuery(id+"F0.wireOp",EDGE,"E7.14.2"),sQuery(id+"F0.wireOp",EDGE,"E7.14.3"),sQuery(id+"F0.wireOp",EDGE,"E7.15.0"),sQuery(id+"F0.wireOp",EDGE,"E7.15.1"),sQuery(id+"F0.wireOp",EDGE,"E7.15.2"),sQuery(id+"F0.wireOp",EDGE,"E7.15.3"),sQuery(id+"F0.wireOp",EDGE,"E7.16.0"),sQuery(id+"F0.wireOp",EDGE,"E7.16.1"),sQuery(id+"F0.wireOp",EDGE,"E7.16.2"),sQuery(id+"F0.wireOp",EDGE,"E7.16.3"),sQuery(id+"F0.wireOp",EDGE,"E7.17.0"),sQuery(id+"F0.wireOp",EDGE,"E7.17.1"),sQuery(id+"F0.wireOp",EDGE,"E7.17.2"),sQuery(id+"F0.wireOp",EDGE,"E7.17.3"),sQuery(id+"F0.wireOp",EDGE,"E7.18.0"),sQuery(id+"F0.wireOp",EDGE,"E7.18.1"),sQuery(id+"F0.wireOp",EDGE,"E7.18.2"),sQuery(id+"F0.wireOp",EDGE,"E7.18.3"),sQuery(id+"F0.wireOp",EDGE,"E7.19.0"),sQuery(id+"F0.wireOp",EDGE,"E7.19.1"),sQuery(id+"F0.wireOp",EDGE,"E7.19.2"),sQuery(id+"F0.wireOp",EDGE,"E7.19.3"),sQuery(id+"F0.wireOp",EDGE,"E7.20.0"),sQuery(id+"F0.wireOp",EDGE,"E7.20.1"),sQuery(id+"F0.wireOp",EDGE,"E7.20.2"),sQuery(id+"F0.wireOp",EDGE,"E7.20.3"),sQuery(id+"F0.wireOp",EDGE,"E7.21.0"),sQuery(id+"F0.wireOp",EDGE,"E7.21.1"),sQuery(id+"F0.wireOp",EDGE,"E7.21.2"),sQuery(id+"F0.wireOp",EDGE,"E7.21.3"),sQuery(id+"F0.wireOp",EDGE,"E7.22.0"),sQuery(id+"F0.wireOp",EDGE,"E7.22.1"),sQuery(id+"F0.wireOp",EDGE,"E7.22.2"),sQuery(id+"F0.wireOp",EDGE,"E7.22.3"),sQuery(id+"F0.wireOp",EDGE,"E7.23.0"),sQuery(id+"F0.wireOp",EDGE,"E7.23.1"),sQuery(id+"F0.wireOp",EDGE,"E7.23.2"),sQuery(id+"F0.wireOp",EDGE,"E7.23.3")])],"isStart":true});
            var sketch = newSketch(context, id + "F4", { "sketchPlane" : qUnion([Q0])});
            skCircle(sketch, "E9", {"center": v(0, 0) * mm, "radius": 39.55 * mm});
            skCircle(sketch, "E10", {"center": v(0, 0) * mm, "radius": 15.88 * mm});
            skLineSegment(sketch, "E11", {"start": v(-3.18, 15.55) * mm, "end": v(-3.18, 39.42) * mm});
            skLineSegment(sketch, "E12", {"start": v(3.18, 15.55) * mm, "end": v(3.18, 39.42) * mm});
            skLineSegment(sketch, "E13.1.0", {"start": v(-11.88, 10.53) * mm, "end": v(-32.56, 22.46) * mm});
            skLineSegment(sketch, "E13.1.1", {"start": v(-15.06, 5.03) * mm, "end": v(-35.73, 16.96) * mm});
            skLineSegment(sketch, "E13.2.0", {"start": v(-15.06, -5.03) * mm, "end": v(-35.73, -16.96) * mm});
            skLineSegment(sketch, "E13.2.1", {"start": v(-11.88, -10.53) * mm, "end": v(-32.56, -22.46) * mm});
            skLineSegment(sketch, "E13.3.0", {"start": v(-3.18, -15.55) * mm, "end": v(-3.18, -39.42) * mm});
            skLineSegment(sketch, "E13.3.1", {"start": v(3.17, -15.55) * mm, "end": v(3.17, -39.42) * mm});
            skLineSegment(sketch, "E13.4.0", {"start": v(11.88, -10.53) * mm, "end": v(32.56, -22.46) * mm});
            skLineSegment(sketch, "E13.4.1", {"start": v(15.06, -5.03) * mm, "end": v(35.73, -16.96) * mm});
            skLineSegment(sketch, "E13.5.0", {"start": v(15.06, 5.03) * mm, "end": v(35.73, 16.96) * mm});
            skLineSegment(sketch, "E13.5.1", {"start": v(11.88, 10.53) * mm, "end": v(32.56, 22.46) * mm});
            skSolve(sketch);
        }
        {
            var Q0;
            {var subQ0=sQuery(id+"F4.wireOp",EDGE,"E11");Q0=makeQuery(id+"F4.imprint","IMPRINT",FACE,{"disambiguationData":[TD([[makeQuery(id+"F4.imprint","IMPRINT",EDGE,{"derivedFrom":subQ0}),1.0]])]});}
            var Q1;
            {var subQ0=sQuery(id+"F4.wireOp",EDGE,"E12");Q1=makeQuery(id+"F4.imprint","IMPRINT",FACE,{"disambiguationData":[TD([[makeQuery(id+"F4.imprint","IMPRINT",EDGE,{"derivedFrom":subQ0}),-1.0]])]});}
            var Q2;
            {var subQ0=sQuery(id+"F4.wireOp",EDGE,"E13.4.1");Q2=makeQuery(id+"F4.imprint","IMPRINT",FACE,{"disambiguationData":[TD([[makeQuery(id+"F4.imprint","IMPRINT",EDGE,{"derivedFrom":subQ0}),1.0]])]});}
            var Q3;
            {var subQ0=sQuery(id+"F4.wireOp",EDGE,"E13.3.1");Q3=makeQuery(id+"F4.imprint","IMPRINT",FACE,{"disambiguationData":[TD([[makeQuery(id+"F4.imprint","IMPRINT",EDGE,{"derivedFrom":subQ0}),1.0]])]});}
            var Q4;
            {var subQ0=sQuery(id+"F4.wireOp",EDGE,"E13.2.1");Q4=makeQuery(id+"F4.imprint","IMPRINT",FACE,{"disambiguationData":[TD([[makeQuery(id+"F4.imprint","IMPRINT",EDGE,{"derivedFrom":subQ0}),1.0]])]});}
            var Q5;
            {var subQ0=sQuery(id+"F4.wireOp",EDGE,"E13.1.1");Q5=makeQuery(id+"F4.imprint","IMPRINT",FACE,{"disambiguationData":[TD([[makeQuery(id+"F4.imprint","IMPRINT",EDGE,{"derivedFrom":subQ0}),1.0]])]});}
            extrude(context, id + "F5", {"entities" : qUnion([Q0, Q1, Q2, Q3, Q4, Q5]), "operationType" : NewBodyOperationType.REMOVE, "oppositeDirection" : true, "depth" : 25.4 * mm});
        }
        {
            var Q0;
            Q0=makeQuery(id+"F1.opExtrude","CAP_FACE",FACE,{"disambiguationData":[OSD([sQuery(id+"F0.wireOp",EDGE,"E1"),sQuery(id+"F0.wireOp",EDGE,"E2"),sQuery(id+"F0.wireOp",EDGE,"E3"),sQuery(id+"F0.wireOp",EDGE,"E4"),sQuery(id+"F0.wireOp",EDGE,"E5"),sQuery(id+"F0.wireOp",EDGE,"E6"),sQuery(id+"F0.wireOp",EDGE,"E7.1.0"),sQuery(id+"F0.wireOp",EDGE,"E7.1.1"),sQuery(id+"F0.wireOp",EDGE,"E7.1.2"),sQuery(id+"F0.wireOp",EDGE,"E7.1.3"),sQuery(id+"F0.wireOp",EDGE,"E7.2.0"),sQuery(id+"F0.wireOp",EDGE,"E7.2.1"),sQuery(id+"F0.wireOp",EDGE,"E7.2.2"),sQuery(id+"F0.wireOp",EDGE,"E7.2.3"),sQuery(id+"F0.wireOp",EDGE,"E7.3.0"),sQuery(id+"F0.wireOp",EDGE,"E7.3.1"),sQuery(id+"F0.wireOp",EDGE,"E7.3.2"),sQuery(id+"F0.wireOp",EDGE,"E7.3.3"),sQuery(id+"F0.wireOp",EDGE,"E7.4.0"),sQuery(id+"F0.wireOp",EDGE,"E7.4.1"),sQuery(id+"F0.wireOp",EDGE,"E7.4.2"),sQuery(id+"F0.wireOp",EDGE,"E7.4.3"),sQuery(id+"F0.wireOp",EDGE,"E7.5.0"),sQuery(id+"F0.wireOp",EDGE,"E7.5.1"),sQuery(id+"F0.wireOp",EDGE,"E7.5.2"),sQuery(id+"F0.wireOp",EDGE,"E7.5.3"),sQuery(id+"F0.wireOp",EDGE,"E7.6.0"),sQuery(id+"F0.wireOp",EDGE,"E7.6.1"),sQuery(id+"F0.wireOp",EDGE,"E7.6.2"),sQuery(id+"F0.wireOp",EDGE,"E7.6.3"),sQuery(id+"F0.wireOp",EDGE,"E7.7.0"),sQuery(id+"F0.wireOp",EDGE,"E7.7.1"),sQuery(id+"F0.wireOp",EDGE,"E7.7.2"),sQuery(id+"F0.wireOp",EDGE,"E7.7.3"),sQuery(id+"F0.wireOp",EDGE,"E7.8.0"),sQuery(id+"F0.wireOp",EDGE,"E7.8.1"),sQuery(id+"F0.wireOp",EDGE,"E7.8.2"),sQuery(id+"F0.wireOp",EDGE,"E7.8.3"),sQuery(id+"F0.wireOp",EDGE,"E7.9.0"),sQuery(id+"F0.wireOp",EDGE,"E7.9.1"),sQuery(id+"F0.wireOp",EDGE,"E7.9.2"),sQuery(id+"F0.wireOp",EDGE,"E7.9.3"),sQuery(id+"F0.wireOp",EDGE,"E7.10.0"),sQuery(id+"F0.wireOp",EDGE,"E7.10.1"),sQuery(id+"F0.wireOp",EDGE,"E7.10.2"),sQuery(id+"F0.wireOp",EDGE,"E7.10.3"),sQuery(id+"F0.wireOp",EDGE,"E7.11.0"),sQuery(id+"F0.wireOp",EDGE,"E7.11.1"),sQuery(id+"F0.wireOp",EDGE,"E7.11.2"),sQuery(id+"F0.wireOp",EDGE,"E7.11.3"),sQuery(id+"F0.wireOp",EDGE,"E7.12.0"),sQuery(id+"F0.wireOp",EDGE,"E7.12.1"),sQuery(id+"F0.wireOp",EDGE,"E7.12.2"),sQuery(id+"F0.wireOp",EDGE,"E7.12.3"),sQuery(id+"F0.wireOp",EDGE,"E7.13.0"),sQuery(id+"F0.wireOp",EDGE,"E7.13.1"),sQuery(id+"F0.wireOp",EDGE,"E7.13.2"),sQuery(id+"F0.wireOp",EDGE,"E7.13.3"),sQuery(id+"F0.wireOp",EDGE,"E7.14.0"),sQuery(id+"F0.wireOp",EDGE,"E7.14.1"),sQuery(id+"F0.wireOp",EDGE,"E7.14.2"),sQuery(id+"F0.wireOp",EDGE,"E7.14.3"),sQuery(id+"F0.wireOp",EDGE,"E7.15.0"),sQuery(id+"F0.wireOp",EDGE,"E7.15.1"),sQuery(id+"F0.wireOp",EDGE,"E7.15.2"),sQuery(id+"F0.wireOp",EDGE,"E7.15.3"),sQuery(id+"F0.wireOp",EDGE,"E7.16.0"),sQuery(id+"F0.wireOp",EDGE,"E7.16.1"),sQuery(id+"F0.wireOp",EDGE,"E7.16.2"),sQuery(id+"F0.wireOp",EDGE,"E7.16.3"),sQuery(id+"F0.wireOp",EDGE,"E7.17.0"),sQuery(id+"F0.wireOp",EDGE,"E7.17.1"),sQuery(id+"F0.wireOp",EDGE,"E7.17.2"),sQuery(id+"F0.wireOp",EDGE,"E7.17.3"),sQuery(id+"F0.wireOp",EDGE,"E7.18.0"),sQuery(id+"F0.wireOp",EDGE,"E7.18.1"),sQuery(id+"F0.wireOp",EDGE,"E7.18.2"),sQuery(id+"F0.wireOp",EDGE,"E7.18.3"),sQuery(id+"F0.wireOp",EDGE,"E7.19.0"),sQuery(id+"F0.wireOp",EDGE,"E7.19.1"),sQuery(id+"F0.wireOp",EDGE,"E7.19.2"),sQuery(id+"F0.wireOp",EDGE,"E7.19.3"),sQuery(id+"F0.wireOp",EDGE,"E7.20.0"),sQuery(id+"F0.wireOp",EDGE,"E7.20.1"),sQuery(id+"F0.wireOp",EDGE,"E7.20.2"),sQuery(id+"F0.wireOp",EDGE,"E7.20.3"),sQuery(id+"F0.wireOp",EDGE,"E7.21.0"),sQuery(id+"F0.wireOp",EDGE,"E7.21.1"),sQuery(id+"F0.wireOp",EDGE,"E7.21.2"),sQuery(id+"F0.wireOp",EDGE,"E7.21.3"),sQuery(id+"F0.wireOp",EDGE,"E7.22.0"),sQuery(id+"F0.wireOp",EDGE,"E7.22.1"),sQuery(id+"F0.wireOp",EDGE,"E7.22.2"),sQuery(id+"F0.wireOp",EDGE,"E7.22.3"),sQuery(id+"F0.wireOp",EDGE,"E7.23.0"),sQuery(id+"F0.wireOp",EDGE,"E7.23.1"),sQuery(id+"F0.wireOp",EDGE,"E7.23.2"),sQuery(id+"F0.wireOp",EDGE,"E7.23.3")])],"isStart":true});
            var sketch = newSketch(context, id + "F6", { "sketchPlane" : qUnion([Q0])});
            skCircle(sketch, "E14", {"center": v(0, 0) * mm, "radius": 42.73 * mm});
            skCircle(sketch, "E15", {"center": v(0, 0) * mm, "radius": 39.55 * mm});
            skSolve(sketch);
        }
        {
            var Q0;
            Q0=makeQuery(id+"F6.imprint","IMPRINT",FACE,{"disambiguationData":[TD([[makeQuery(id+"F6.imprint","IMPRINT",EDGE,{"derivedFrom":sQuery(id+"F6.wireOp",EDGE,"E14")}),1.0]])]});
            extrude(context, id + "F7", {"entities" : qUnion([Q0]), "operationType" : NewBodyOperationType.ADD, "depth" : 9.52 * mm});
        }
        {
            var Q0;
            Q0=qCreatedBy(makeId("Right.planeOp"),FACE);
            var sketch = newSketch(context, id + "F8", { "sketchPlane" : qUnion([Q0])});
            skCircle(sketch, "E16", {"center": v(15.88, 0) * mm, "radius": 1.59 * mm});
            skSolve(sketch);
        }
        {
            var Q0;
            Q0=makeQuery(id+"F8.imprint","IMPRINT",FACE,{"disambiguationData":[TD([[makeQuery(id+"F8.imprint","IMPRINT",EDGE,{"derivedFrom":sQuery(id+"F8.wireOp",EDGE,"E16")}),1.0]])]});
            extrude(context, id + "F9", {"entities" : qUnion([Q0]), "operationType" : NewBodyOperationType.REMOVE, "endBound" : BoundingType.SYMMETRIC, "depth" : 127 * mm});
        }
    });
